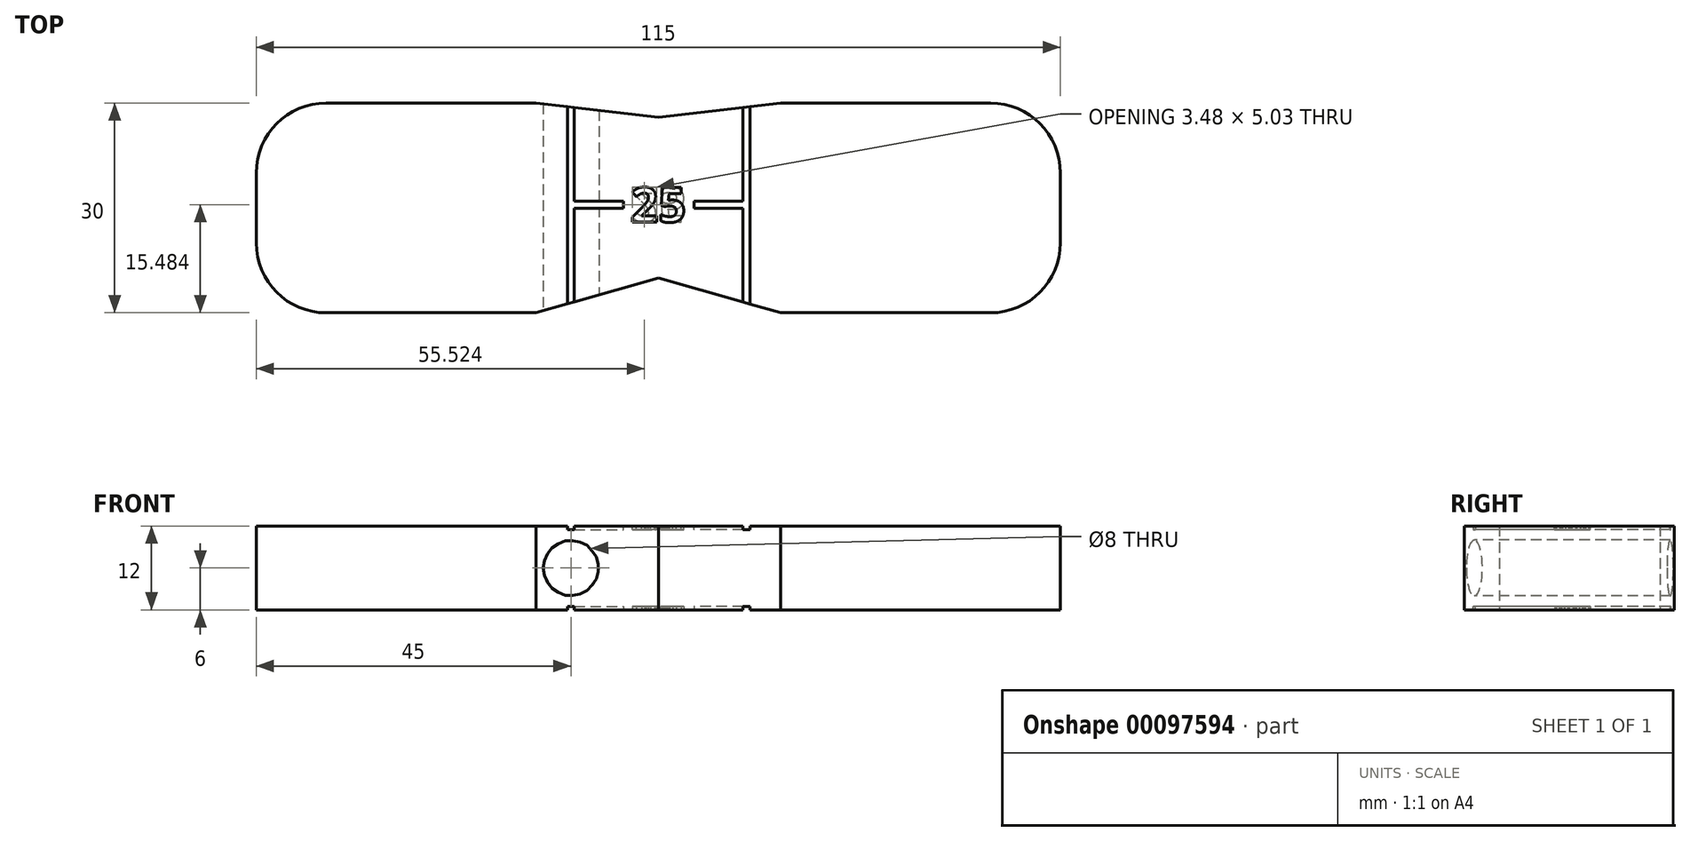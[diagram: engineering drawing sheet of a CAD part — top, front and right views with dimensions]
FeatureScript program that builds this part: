
annotation { "Feature Type Name" : "Feature", "Feature Type Description" : "" }
export const myFeature = defineFeature(function(context is Context, id is Id, definition is map)
    precondition{}
    {
        {
            var Q0;
            Q0=qCreatedBy(makeId("Top.planeOp"),FACE);
            var sketch = newSketch(context, id + "F0", { "sketchPlane" : qUnion([Q0])});
            skLineSegment(sketch, "E0", {"start": v(0, 0) * mm, "end": v(0, 30) * mm});
            skLineSegment(sketch, "E1", {"start": v(35, 30) * mm, "end": v(35, 0) * mm});
            skLineSegment(sketch, "E2", {"start": v(35, 0) * mm, "end": v(17.5, 5) * mm});
            skLineSegment(sketch, "E3", {"start": v(17.5, 5) * mm, "end": v(0, 0) * mm});
            skLineSegment(sketch, "E4", {"start": v(0, 30) * mm, "end": v(17.5, 28) * mm});
            skLineSegment(sketch, "E5", {"start": v(17.5, 28) * mm, "end": v(35, 30) * mm});
            skLineSegment(sketch, "E6", {"start": v(0, 15) * mm, "end": v(35, 15) * mm, "construction": true});
            skLineSegment(sketch, "E7", {"start": v(17.5, 15) * mm, "end": v(17.5, 30) * mm, "construction": true});
            skLineSegment(sketch, "E8", {"start": v(17.5, 15) * mm, "end": v(17.5, 0) * mm, "construction": true});
            skLineSegment(sketch, "E9.bottom", {"start": v(35, 30) * mm, "end": v(65, 30) * mm});
            skLineSegment(sketch, "E9.top", {"start": v(35, 0) * mm, "end": v(65, 0) * mm});
            skLineSegment(sketch, "E9.right", {"start": v(75, 20) * mm, "end": v(75, 10) * mm});
            skPoint(sketch, "E10.visualSharp", {"position": v(75, 30) * mm});
            skArc(sketch, "E10.filletArc", {"start": v(75, 20) * mm, "mid": v(72.07, 27.07) * mm, "end": v(65, 30) * mm});
            skPoint(sketch, "E11.visualSharp", {"position": v(75, 0) * mm});
            skArc(sketch, "E11.filletArc", {"start": v(65, 0) * mm, "mid": v(72.07, 2.93) * mm, "end": v(75, 10) * mm});
            skLineSegment(sketch, "E12.MirrorCS", {"start": v(0, 30) * mm, "end": v(-30, 30) * mm});
            skArc(sketch, "E13.MirrorCS", {"start": v(-40, 20) * mm, "mid": v(-37.07, 27.07) * mm, "end": v(-30, 30) * mm});
            skLineSegment(sketch, "E14.MirrorCS", {"start": v(-40, 20) * mm, "end": v(-40, 10) * mm});
            skArc(sketch, "E15.MirrorCS", {"start": v(-30, 0) * mm, "mid": v(-37.07, 2.93) * mm, "end": v(-40, 10) * mm});
            skLineSegment(sketch, "E16.MirrorCS", {"start": v(0, 0) * mm, "end": v(-30, 0) * mm});
            skSolve(sketch);
        }
        {
            var Q0;
            Q0 = qSketchRegion(id + "F0", true);
            extrude(context, id + "F1", {"entities" : qUnion([Q0]), "depth" : 12 * mm, "offsetDistance" : 25 * mm});
        }
        {
            var Q0;
            Q0=qCreatedBy(makeId("Front.planeOp"),FACE);
            var sketch = newSketch(context, id + "F2", { "sketchPlane" : qUnion([Q0])});
            skCircle(sketch, "E17", {"center": v(5, 6) * mm, "radius": 4 * mm});
            skLineSegment(sketch, "E18", {"start": v(0, 6) * mm, "end": v(17.55, 6) * mm, "construction": true});
            skLineSegment(sketch, "E19", {"start": v(17.55, 0) * mm, "end": v(17.55, 12) * mm, "construction": true});
            skLineSegment(sketch, "E20", {"start": v(5, 0) * mm, "end": v(5, 10) * mm, "construction": true});
            skLineSegment(sketch, "E21.bottom", {"start": v(4.5, 0) * mm, "end": v(5.5, 0) * mm});
            skLineSegment(sketch, "E21.top", {"start": v(4.5, 0.5) * mm, "end": v(5.5, 0.5) * mm});
            skLineSegment(sketch, "E21.left", {"start": v(4.5, 0) * mm, "end": v(4.5, 0.5) * mm});
            skLineSegment(sketch, "E21.right", {"start": v(5.5, 0) * mm, "end": v(5.5, 0.5) * mm});
            skCircle(sketch, "E22.MirrorC", {"center": v(30.1, 6) * mm, "radius": 4 * mm});
            skLineSegment(sketch, "E23.MirrorCS", {"start": v(30.6, 0.5) * mm, "end": v(29.6, 0.5) * mm});
            skLineSegment(sketch, "E24.MirrorCS", {"start": v(29.6, 0) * mm, "end": v(29.6, 0.5) * mm});
            skLineSegment(sketch, "E25.MirrorCS", {"start": v(30.6, 0) * mm, "end": v(29.6, 0) * mm});
            skLineSegment(sketch, "E26.MirrorCS", {"start": v(30.6, 0) * mm, "end": v(30.6, 0.5) * mm});
            skLineSegment(sketch, "E27.MirrorCS", {"start": v(4.5, 12) * mm, "end": v(5.5, 12) * mm});
            skLineSegment(sketch, "E28.MirrorCS", {"start": v(5.5, 12) * mm, "end": v(5.5, 11.5) * mm});
            skLineSegment(sketch, "E29.MirrorCS", {"start": v(4.5, 11.5) * mm, "end": v(5.5, 11.5) * mm});
            skLineSegment(sketch, "E30.MirrorCS", {"start": v(4.5, 12) * mm, "end": v(4.5, 11.5) * mm});
            skLineSegment(sketch, "E31.MirrorCS", {"start": v(30.6, 11.5) * mm, "end": v(29.6, 11.5) * mm});
            skLineSegment(sketch, "E32.MirrorCS", {"start": v(29.6, 12) * mm, "end": v(29.6, 11.5) * mm});
            skLineSegment(sketch, "E33.MirrorCS", {"start": v(30.6, 12) * mm, "end": v(30.6, 11.5) * mm});
            skLineSegment(sketch, "E34.MirrorCS", {"start": v(30.6, 12) * mm, "end": v(29.6, 12) * mm});
            skSolve(sketch);
        }
        {
            var Q0;
            Q0=makeQuery(id+"F2.imprint","IMPRINT",FACE,{"disambiguationData":[TD([[makeQuery(id+"F2.imprint","IMPRINT",EDGE,{"derivedFrom":sQuery(id+"F2.wireOp",EDGE,"E17")}),1.0]])]});
            var Q1;
            Q1=makeQuery(id+"F2.imprint","IMPRINT",FACE,{"disambiguationData":[TD([[makeQuery(id+"F2.imprint","IMPRINT",EDGE,{"derivedFrom":sQuery(id+"F2.wireOp",EDGE,"E21.bottom")}),1.0]])]});
            var Q2;
            Q2=makeQuery(id+"F2.imprint","IMPRINT",FACE,{"disambiguationData":[TD([[makeQuery(id+"F2.imprint","IMPRINT",EDGE,{"derivedFrom":sQuery(id+"F2.wireOp",EDGE,"E22.MirrorC")}),-1.0]])]});
            var Q3;
            Q3=makeQuery(id+"F2.imprint","IMPRINT",FACE,{"disambiguationData":[TD([[makeQuery(id+"F2.imprint","IMPRINT",EDGE,{"derivedFrom":sQuery(id+"F2.wireOp",EDGE,"E23.MirrorCS")}),1.0]])]});
            var Q4;
            Q4=makeQuery(id+"F2.imprint","IMPRINT",FACE,{"disambiguationData":[TD([[makeQuery(id+"F2.imprint","IMPRINT",EDGE,{"derivedFrom":sQuery(id+"F2.wireOp",EDGE,"E31.MirrorCS")}),-1.0]])]});
            var Q5;
            Q5=makeQuery(id+"F2.imprint","IMPRINT",FACE,{"disambiguationData":[TD([[makeQuery(id+"F2.imprint","IMPRINT",EDGE,{"derivedFrom":sQuery(id+"F2.wireOp",EDGE,"E27.MirrorCS")}),-1.0]])]});
            extrude(context, id + "F3", {"entities" : qUnion([Q0, Q1, Q2, Q3, Q4, Q5]), "operationType" : NewBodyOperationType.REMOVE, "endBound" : BoundingType.THROUGH_ALL, "oppositeDirection" : true, "depth" : 25 * mm, "offsetDistance" : 25 * mm});
        }
        {
            var Q0;
            {var subQ0=sQuery(id+"F0.wireOp",EDGE,"E5");var subQ1=sQuery(id+"F0.wireOp",EDGE,"E4");var subQ2=sQuery(id+"F0.wireOp",EDGE,"E3");var subQ3=sQuery(id+"F0.wireOp",EDGE,"E2");Q0=makeQuery(id+"F3.boolean.opBoolean","SPLIT",FACE,{"disambiguationData":[TD([makeQuery(id+"F3.opExtrude","SWEPT_FACE",FACE,{"disambiguationData":[OSD([sQuery(id+"F2.wireOp",EDGE,"E21.right")])]})])],"derivedFrom":makeQuery(id+"F1.opExtrude","CAP_FACE",FACE,{"disambiguationData":[OSD([sQuery(id+"F0.wireOp",EDGE,"E0"),sQuery(id+"F0.wireOp",EDGE,"E1"),subQ3,subQ2,subQ1,subQ0])],"isStart":true})});}
            var sketch = newSketch(context, id + "F4", { "sketchPlane" : qUnion([Q0])});
            skText(sketch, "E35", { "text": "25", "fontName": "OpenSans-Bold.ttf"});
            skLineSegment(sketch, "E36", {"start": v(5.5, -15.47) * mm, "end": v(29.6, -15.47) * mm, "construction": true});
            skLineSegment(sketch, "E37", {"start": v(13.52, -15.47) * mm, "end": v(17.55, -15.47) * mm, "construction": true});
            skLineSegment(sketch, "E38.bottom", {"start": v(29.6, -14.97) * mm, "end": v(22.6, -14.97) * mm});
            skLineSegment(sketch, "E38.top", {"start": v(29.6, -15.97) * mm, "end": v(22.6, -15.97) * mm});
            skLineSegment(sketch, "E38.left", {"start": v(29.6, -14.97) * mm, "end": v(29.6, -15.97) * mm});
            skLineSegment(sketch, "E38.right", {"start": v(22.6, -14.97) * mm, "end": v(22.6, -15.97) * mm});
            skLineSegment(sketch, "E39.MirrorCS", {"start": v(5.5, -14.97) * mm, "end": v(12.5, -14.97) * mm});
            skLineSegment(sketch, "E40.MirrorCS", {"start": v(12.5, -14.97) * mm, "end": v(12.5, -15.97) * mm});
            skLineSegment(sketch, "E41.MirrorCS", {"start": v(5.5, -15.97) * mm, "end": v(12.5, -15.97) * mm});
            skLineSegment(sketch, "E42.MirrorCS", {"start": v(5.5, -14.97) * mm, "end": v(5.5, -15.97) * mm});
            const initialGuessF4  = {"E35": [0.01352, -0.01797, 1, 0, 0.005]};
            skSetInitialGuess(sketch, initialGuessF4);
            skSolve(sketch);
        }
        {
            var Q0;
            Q0=makeQuery(id+"F4.imprint","IMPRINT",FACE,{"disambiguationData":[TD([[makeQuery(id+"F4.imprint","IMPRINT",EDGE,{"derivedFrom":sQuery(id+"F4.wireOp",EDGE,"E39.MirrorCS")}),-1.0]])]});
            var Q1;
            Q1=makeQuery(id+"F4.imprint","IMPRINT",FACE,{"disambiguationData":[TD([[makeQuery(id+"F4.imprint","IMPRINT",EDGE,{"derivedFrom":sQuery(id+"F4.wireOp",EDGE,"E35.sketch_text.stroke-0")}),-1.0]])]});
            var Q2;
            Q2=makeQuery(id+"F4.imprint","IMPRINT",FACE,{"disambiguationData":[TD([[makeQuery(id+"F4.imprint","IMPRINT",EDGE,{"derivedFrom":sQuery(id+"F4.wireOp",EDGE,"E35.sketch_text.stroke-24")}),-1.0]])]});
            var Q3;
            Q3=makeQuery(id+"F4.imprint","IMPRINT",FACE,{"disambiguationData":[TD([[makeQuery(id+"F4.imprint","IMPRINT",EDGE,{"derivedFrom":sQuery(id+"F4.wireOp",EDGE,"E38.bottom")}),1.0]])]});
            extrude(context, id + "F5", {"entities" : qUnion([Q0, Q1, Q2, Q3]), "operationType" : NewBodyOperationType.REMOVE, "oppositeDirection" : true, "depth" : 0.5 * mm, "offsetDistance" : 25 * mm});
        }
        {
            var Q0;
            Q0=qCreatedBy(makeId("Top.planeOp"),FACE);
            cPlane(context, id + "F6", {"entities" : qUnion([Q0]), "cplaneType" : CPlaneType.OFFSET, "offset" : 12 * mm, "width" : 150 * mm, "height" : 150 * mm});
        }
        {
            var Q0;
            Q0=qCreatedBy(id+"F6.planeOp",FACE);
            var sketch = newSketch(context, id + "F7", { "sketchPlane" : qUnion([Q0])});
            skLineSegment(sketch, "E43", {"start": v(5.5, 15.47) * mm, "end": v(29.6, 15.47) * mm, "construction": true});
            skText(sketch, "E44", { "text": "25", "fontName": "OpenSans-Bold.ttf"});
            skLineSegment(sketch, "E45", {"start": v(13.52, 15.47) * mm, "end": v(17.55, 15.47) * mm, "construction": true});
            skLineSegment(sketch, "E46.bottom", {"start": v(5.5, 15.97) * mm, "end": v(12.5, 15.97) * mm});
            skLineSegment(sketch, "E46.top", {"start": v(5.5, 14.97) * mm, "end": v(12.5, 14.97) * mm});
            skLineSegment(sketch, "E46.left", {"start": v(5.5, 15.97) * mm, "end": v(5.5, 14.97) * mm});
            skLineSegment(sketch, "E46.right", {"start": v(12.5, 15.97) * mm, "end": v(12.5, 14.97) * mm});
            skLineSegment(sketch, "E47.MirrorCS", {"start": v(22.6, 15.97) * mm, "end": v(22.6, 14.97) * mm});
            skLineSegment(sketch, "E48.MirrorCS", {"start": v(29.6, 15.97) * mm, "end": v(22.6, 15.97) * mm});
            skLineSegment(sketch, "E49.MirrorCS", {"start": v(29.6, 14.97) * mm, "end": v(22.6, 14.97) * mm});
            skLineSegment(sketch, "E50.MirrorCS", {"start": v(29.6, 15.97) * mm, "end": v(29.6, 14.97) * mm});
            const initialGuessF7  = {"E44": [0.01352, 0.01297, 1, 0, 0.005]};
            skSetInitialGuess(sketch, initialGuessF7);
            skSolve(sketch);
        }
        {
            var Q0;
            Q0 = qSketchRegion(id + "F7", true);
            extrude(context, id + "F8", {"entities" : qUnion([Q0]), "operationType" : NewBodyOperationType.REMOVE, "oppositeDirection" : true, "depth" : 0.5 * mm, "offsetDistance" : 25 * mm});
        }
    });
